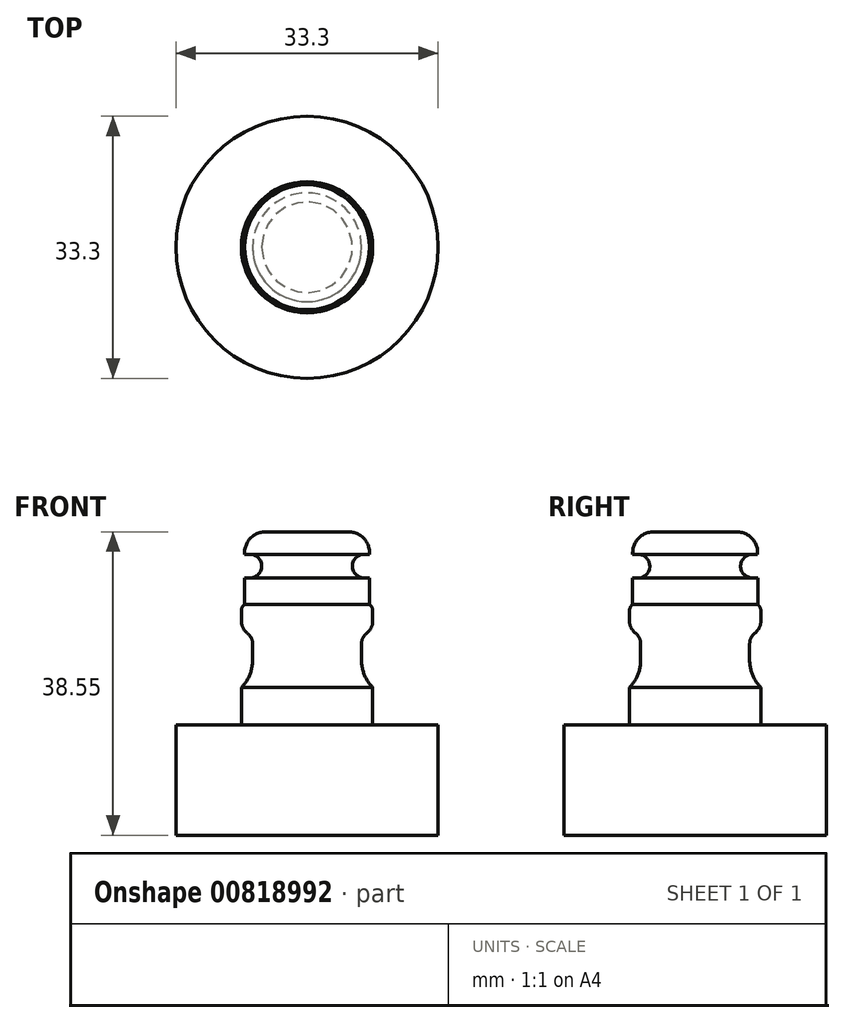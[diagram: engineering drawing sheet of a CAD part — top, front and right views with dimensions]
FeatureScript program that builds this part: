
annotation { "Feature Type Name" : "Feature", "Feature Type Description" : "" }
export const myFeature = defineFeature(function(context is Context, id is Id, definition is map)
    precondition{}
    {
        {
            var Q0;
            Q0=qCreatedBy(makeId("Front.planeOp"),FACE);
            var sketch = newSketch(context, id + "F0", { "sketchPlane" : qUnion([Q0])});
            skLineSegment(sketch, "E0", {"start": v(0, 0) * mm, "end": v(-16.65, 0) * mm});
            skLineSegment(sketch, "E1", {"start": v(-16.65, 0) * mm, "end": v(-16.65, 14) * mm});
            skLineSegment(sketch, "E2", {"start": v(-16.65, 14) * mm, "end": v(-8.34, 14) * mm});
            skLineSegment(sketch, "E3", {"start": v(-8.34, 14) * mm, "end": v(-8.34, 18.76) * mm});
            skLineSegment(sketch, "E4", {"start": v(-8.34, 18.76) * mm, "end": v(-6.92, 18.76) * mm});
            skLineSegment(sketch, "E5", {"start": v(-6.92, 18.76) * mm, "end": v(-6.92, 26) * mm});
            skLineSegment(sketch, "E6", {"start": v(-6.92, 26) * mm, "end": v(-8.34, 26) * mm});
            skLineSegment(sketch, "E7", {"start": v(-8.34, 26) * mm, "end": v(-8.34, 29.3) * mm});
            skLineSegment(sketch, "E8", {"start": v(-8.34, 29.3) * mm, "end": v(-7.96, 29.3) * mm});
            skLineSegment(sketch, "E9", {"start": v(-7.96, 29.3) * mm, "end": v(-7.96, 32.7) * mm});
            skLineSegment(sketch, "E10", {"start": v(-7.96, 32.7) * mm, "end": v(-5.77, 32.7) * mm});
            skLineSegment(sketch, "E11", {"start": v(-5.77, 32.7) * mm, "end": v(-5.77, 35.7) * mm});
            skLineSegment(sketch, "E12", {"start": v(-5.77, 35.7) * mm, "end": v(-7.93, 35.7) * mm});
            skLineSegment(sketch, "E13", {"start": v(-7.93, 35.7) * mm, "end": v(-7.93, 38.55) * mm});
            skLineSegment(sketch, "E14", {"start": v(-7.93, 38.55) * mm, "end": v(0, 38.55) * mm});
            skLineSegment(sketch, "E15", {"start": v(0, 38.55) * mm, "end": v(0, 0) * mm});
            skSolve(sketch);
        }
        {
            var Q0;
            Q0=makeQuery(id+"F0.imprint","IMPRINT",FACE,{"disambiguationData":[TD([[makeQuery(id+"F0.imprint","IMPRINT",EDGE,{"derivedFrom":sQuery(id+"F0.wireOp",EDGE,"E0")}),-1.0]])]});
            var Q1;
            Q1=sQuery(id+"F0.wireOp",EDGE,"E15");
            revolve(context, id + "F1", {"surfaceOperationType" : NewSurfaceOperationType.NEW, "entities" : qUnion([Q0]), "axis" : qUnion([Q1]), "revolveType" : RevolveType.FULL});
        }
        {
            var Q0;
            Q0=makeQuery(id+"F1.opRevolve","SWEPT_EDGE",EDGE,{"disambiguationData":[OSD([sQuery(id+"F0.wireOp",EDGE,"E10"),sQuery(id+"F0.wireOp",EDGE,"E11")])]});
            var Q1;
            Q1=makeQuery(id+"F1.opRevolve","SWEPT_EDGE",EDGE,{"disambiguationData":[OSD([sQuery(id+"F0.wireOp",EDGE,"E11"),sQuery(id+"F0.wireOp",EDGE,"E12")])]});
            fillet(context, id + "F2", {"entities" : qUnion([Q0, Q1]), "radius" : 1.5 * mm, "tangentPropagation" : true, "allowEdgeOverflow" : false});
        }
        {
            var Q0;
            Q0=makeQuery(id+"F1.opRevolve","SWEPT_EDGE",EDGE,{"disambiguationData":[OSD([sQuery(id+"F0.wireOp",EDGE,"E5"),sQuery(id+"F0.wireOp",EDGE,"E6")])]});
            fillet(context, id + "F3", {"entities" : qUnion([Q0]), "radius" : 1.69 * mm, "tangentPropagation" : true, "allowEdgeOverflow" : false});
        }
        {
            var Q0;
            Q0=makeQuery(id+"F1.opRevolve","SWEPT_EDGE",EDGE,{"disambiguationData":[OSD([sQuery(id+"F0.wireOp",EDGE,"E7"),sQuery(id+"F0.wireOp",EDGE,"E8")])]});
            fillet(context, id + "F4", {"entities" : qUnion([Q0]), "radius" : 0.97 * mm, "tangentPropagation" : true, "allowEdgeOverflow" : false});
        }
        {
            var Q0;
            Q0=makeQuery(id+"F1.opRevolve","SWEPT_EDGE",EDGE,{"disambiguationData":[OSD([sQuery(id+"F0.wireOp",EDGE,"E4"),sQuery(id+"F0.wireOp",EDGE,"E5")])]});
            fillet(context, id + "F5", {"entities" : qUnion([Q0]), "radius" : 5 * mm, "tangentPropagation" : true, "allowEdgeOverflow" : false});
        }
        {
            var Q0;
            Q0=makeQuery(id+"F3.opFillet","BLEND_EDGE",EDGE,{"blendedFrom":[makeQuery(id+"F1.opRevolve","SWEPT_EDGE",EDGE,{"disambiguationData":[OSD([sQuery(id+"F0.wireOp",EDGE,"E5"),sQuery(id+"F0.wireOp",EDGE,"E6")])]}),makeQuery(id+"F1.opRevolve","SWEPT_FACE",FACE,{"disambiguationData":[OSD([sQuery(id+"F0.wireOp",EDGE,"E7")])]})],"blendedInto":[makeQuery(id+"F1.opRevolve","SWEPT_FACE",FACE,{"disambiguationData":[OSD([sQuery(id+"F0.wireOp",EDGE,"E7")])]})]});
            fillet(context, id + "F6", {"entities" : qUnion([Q0]), "radius" : 1.92 * mm, "tangentPropagation" : true, "allowEdgeOverflow" : false});
        }
        {
            var Q0;
            Q0=makeQuery(id+"F1.opRevolve","SWEPT_EDGE",EDGE,{"disambiguationData":[OSD([sQuery(id+"F0.wireOp",EDGE,"E13"),sQuery(id+"F0.wireOp",EDGE,"E14")])]});
            fillet(context, id + "F7", {"entities" : qUnion([Q0]), "radius" : 2.66 * mm, "tangentPropagation" : true, "allowEdgeOverflow" : false});
        }
    });
